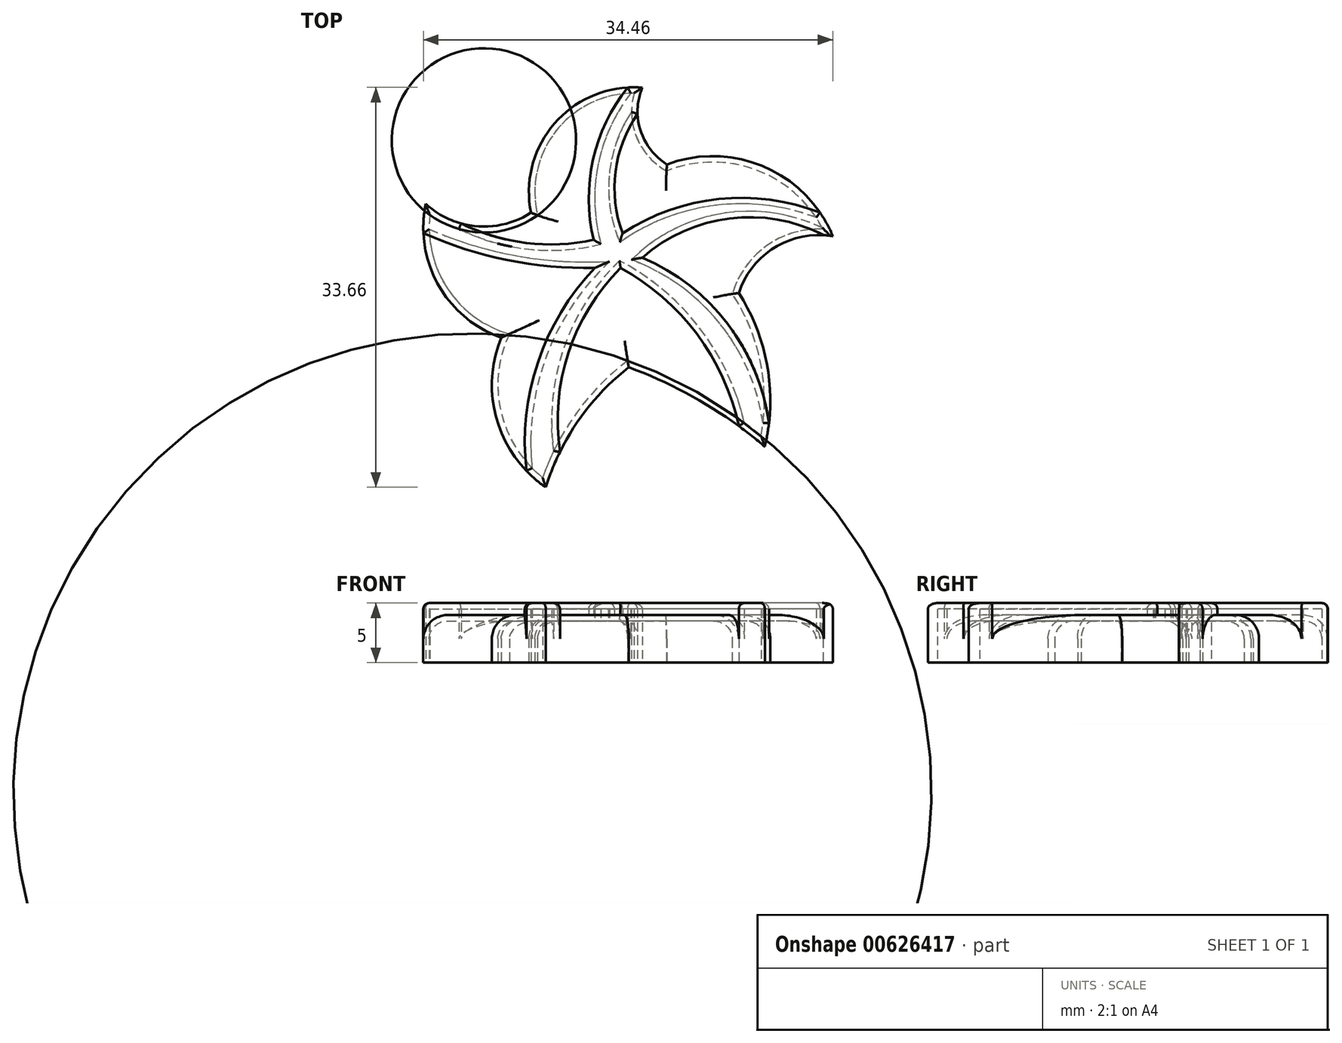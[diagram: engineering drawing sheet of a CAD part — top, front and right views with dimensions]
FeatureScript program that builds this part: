
annotation { "Feature Type Name" : "Feature", "Feature Type Description" : "" }
export const myFeature = defineFeature(function(context is Context, id is Id, definition is map)
    precondition{}
    {
        {
            var Q0;
            Q0=qCreatedBy(makeId("Top.planeOp"),FACE);
            var sketch = newSketch(context, id + "F0", { "sketchPlane" : qUnion([Q0])});
            skArc(sketch, "E0", {"start": v(-51.1, 49.73) * mm, "mid": v(-58.41, 46.8) * mm, "end": v(-60.47, 39.21) * mm});
            skArc(sketch, "E1", {"start": v(-51.1, 49.73) * mm, "mid": v(-51.25, 46.11) * mm, "end": v(-49.02, 43.27) * mm});
            skArc(sketch, "E2", {"start": v(-35.07, 37.23) * mm, "mid": v(-40.83, 43.06) * mm, "end": v(-49.02, 43.27) * mm});
            skArc(sketch, "E3", {"start": v(-35.07, 37.23) * mm, "mid": v(-39.91, 36.3) * mm, "end": v(-42.98, 32.44) * mm});
            skArc(sketch, "E4", {"start": v(-40.8, 19.53) * mm, "mid": v(-40.57, 26.21) * mm, "end": v(-42.98, 32.44) * mm});
            skArc(sketch, "E5", {"start": v(-40.8, 19.53) * mm, "mid": v(-46.23, 23.36) * mm, "end": v(-52.25, 26.2) * mm});
            skArc(sketch, "E6", {"start": v(-52.25, 26.2) * mm, "mid": v(-56.5, 21.68) * mm, "end": v(-59.22, 16.1) * mm});
            skArc(sketch, "E7", {"start": v(-62.97, 28.7) * mm, "mid": v(-63.33, 21.73) * mm, "end": v(-59.22, 16.1) * mm});
            skArc(sketch, "E8", {"start": v(-69.32, 39.94) * mm, "mid": v(-68.27, 33.12) * mm, "end": v(-62.97, 28.7) * mm});
            skArc(sketch, "E9", {"start": v(-69.32, 39.94) * mm, "mid": v(-65.02, 38.06) * mm, "end": v(-60.47, 39.21) * mm});
            skSolve(sketch);
        }
        {
            var Q0;
            Q0=makeQuery(id+"F0.imprint","IMPRINT",FACE,{"disambiguationData":[TD([[makeQuery(id+"F0.imprint","IMPRINT",EDGE,{"derivedFrom":sQuery(id+"F0.wireOp",EDGE,"E0")}),1.0]])]});
            extrude(context, id + "F1", {"entities" : qUnion([Q0]), "depth" : 4 * mm, "offsetDistance" : 25 * mm});
        }
        {
            var Q0;
            Q0=makeQuery(id+"F1.opExtrude","CAP_FACE",FACE,{"disambiguationData":[OSD([sQuery(id+"F0.wireOp",EDGE,"E0"),sQuery(id+"F0.wireOp",EDGE,"E1"),sQuery(id+"F0.wireOp",EDGE,"E2"),sQuery(id+"F0.wireOp",EDGE,"E3"),sQuery(id+"F0.wireOp",EDGE,"E4"),sQuery(id+"F0.wireOp",EDGE,"E5"),sQuery(id+"F0.wireOp",EDGE,"E6"),sQuery(id+"F0.wireOp",EDGE,"E7"),sQuery(id+"F0.wireOp",EDGE,"E8"),sQuery(id+"F0.wireOp",EDGE,"E9")])],"isStart":false});
            var sketch = newSketch(context, id + "F2", { "sketchPlane" : qUnion([Q0])});
            skArc(sketch, "E10", {"start": v(-36.15, 39.21) * mm, "mid": v(-44.66, 40.36) * mm, "end": v(-52.76, 37.48) * mm});
            skArc(sketch, "E11", {"start": v(-35.83, 37.32) * mm, "mid": v(-43.76, 38.73) * mm, "end": v(-51.1, 35.42) * mm});
            skArc(sketch, "E12", {"start": v(-40.45, 21.5) * mm, "mid": v(-43.94, 29.87) * mm, "end": v(-51.1, 35.42) * mm});
            skArc(sketch, "E13", {"start": v(-42.98, 21.25) * mm, "mid": v(-46.5, 28.98) * mm, "end": v(-52.93, 34.56) * mm});
            skArc(sketch, "E14", {"start": v(-52.93, 34.56) * mm, "mid": v(-57.32, 27.42) * mm, "end": v(-58.03, 19.07) * mm});
            skArc(sketch, "E15", {"start": v(-55.11, 34.56) * mm, "mid": v(-59.88, 26.66) * mm, "end": v(-60.86, 17.48) * mm});
            skArc(sketch, "E16", {"start": v(-69.52, 37.48) * mm, "mid": v(-62.48, 35.22) * mm, "end": v(-55.11, 34.56) * mm});
            skArc(sketch, "E17", {"start": v(-66.35, 38.3) * mm, "mid": v(-60.9, 36.66) * mm, "end": v(-55.2, 36.93) * mm});
            skPoint(sketch, "E18.visualSharp", {"position": v(-51.1, 49.73) * mm});
            skArc(sketch, "E19", {"start": v(-52.32, 49.74) * mm, "mid": v(-55.25, 43.67) * mm, "end": v(-55.2, 36.93) * mm});
            skArc(sketch, "E20", {"start": v(-51.5, 47.53) * mm, "mid": v(-53.36, 42.66) * mm, "end": v(-52.76, 37.48) * mm});
            skSolve(sketch);
        }
        {
            var Q0;
            {var subQ9=sQuery(id+"F2.wireOp",EDGE,"E10");Q0=makeQuery(id+"F2.imprint","IMPRINT",FACE,{"disambiguationData":[TD([[makeQuery(id+"F2.imprint","IMPRINT",EDGE,{"derivedFrom":subQ9}),1.0]])]});}
            extrude(context, id + "F3", {"entities" : qUnion([Q0]), "operationType" : NewBodyOperationType.ADD, "depth" : 1 * mm, "offsetDistance" : 25 * mm});
        }
        {
            var Q0;
            Q0=makeQuery(id+"F1.opExtrude","CAP_EDGE",EDGE,{"disambiguationData":[OSD([sQuery(id+"F0.wireOp",EDGE,"E6")])],"isStart":false});
            var Q1;
            Q1=makeQuery(id+"F1.opExtrude","CAP_EDGE",EDGE,{"disambiguationData":[OSD([sQuery(id+"F0.wireOp",EDGE,"E5")])],"isStart":false});
            var Q2;
            Q2=makeQuery(id+"F1.opExtrude","CAP_EDGE",EDGE,{"disambiguationData":[OSD([sQuery(id+"F0.wireOp",EDGE,"E4")])],"isStart":false});
            var Q3;
            Q3=makeQuery(id+"F1.opExtrude","CAP_EDGE",EDGE,{"disambiguationData":[OSD([sQuery(id+"F0.wireOp",EDGE,"E3")])],"isStart":false});
            var Q4;
            Q4=makeQuery(id+"F1.opExtrude","CAP_EDGE",EDGE,{"disambiguationData":[OSD([sQuery(id+"F0.wireOp",EDGE,"E8")])],"isStart":false});
            var Q5;
            Q5=makeQuery(id+"F1.opExtrude","CAP_EDGE",EDGE,{"disambiguationData":[OSD([sQuery(id+"F0.wireOp",EDGE,"E7")])],"isStart":false});
            var Q6;
            Q6=makeQuery(id+"F1.opExtrude","CAP_EDGE",EDGE,{"disambiguationData":[OSD([sQuery(id+"F0.wireOp",EDGE,"E9")])],"isStart":false});
            var Q7;
            Q7=makeQuery(id+"F1.opExtrude","CAP_EDGE",EDGE,{"disambiguationData":[OSD([sQuery(id+"F0.wireOp",EDGE,"E0")])],"isStart":false});
            var Q8;
            Q8=makeQuery(id+"F1.opExtrude","CAP_EDGE",EDGE,{"disambiguationData":[OSD([sQuery(id+"F0.wireOp",EDGE,"E1")])],"isStart":false});
            var Q9;
            Q9=makeQuery(id+"F1.opExtrude","CAP_EDGE",EDGE,{"disambiguationData":[OSD([sQuery(id+"F0.wireOp",EDGE,"E2")])],"isStart":false});
            fillet(context, id + "F4", {"entities" : qUnion([Q0, Q1, Q2, Q3, Q4, Q5, Q6, Q7, Q8, Q9]), "radius" : 2 * mm, "tangentPropagation" : true, "allowEdgeOverflow" : false});
        }
        {
            var Q0;
            Q0=makeQuery(id+"F1.opExtrude","CAP_FACE",FACE,{"disambiguationData":[OSD([sQuery(id+"F0.wireOp",EDGE,"E0"),sQuery(id+"F0.wireOp",EDGE,"E1"),sQuery(id+"F0.wireOp",EDGE,"E2"),sQuery(id+"F0.wireOp",EDGE,"E3"),sQuery(id+"F0.wireOp",EDGE,"E4"),sQuery(id+"F0.wireOp",EDGE,"E5"),sQuery(id+"F0.wireOp",EDGE,"E6"),sQuery(id+"F0.wireOp",EDGE,"E7"),sQuery(id+"F0.wireOp",EDGE,"E8"),sQuery(id+"F0.wireOp",EDGE,"E9")])],"isStart":true});
            shell(context, id + "F5", {"entities" : qUnion([Q0]), "thickness" : 0.5 * mm});
        }
        {
            var Q0;
            Q0=makeQuery(id+"F3.opExtrude","CAP_FACE",FACE,{"disambiguationData":[OSD([sQuery(id+"F0.wireOp",EDGE,"E0"),sQuery(id+"F0.wireOp",EDGE,"E2"),sQuery(id+"F0.wireOp",EDGE,"E3"),sQuery(id+"F0.wireOp",EDGE,"E4"),sQuery(id+"F0.wireOp",EDGE,"E5"),sQuery(id+"F0.wireOp",EDGE,"E6"),sQuery(id+"F0.wireOp",EDGE,"E7"),sQuery(id+"F0.wireOp",EDGE,"E8"),sQuery(id+"F0.wireOp",EDGE,"E9"),sQuery(id+"F2.wireOp",EDGE,"E10"),sQuery(id+"F2.wireOp",EDGE,"E11"),sQuery(id+"F2.wireOp",EDGE,"E12"),sQuery(id+"F2.wireOp",EDGE,"E13"),sQuery(id+"F2.wireOp",EDGE,"E14"),sQuery(id+"F2.wireOp",EDGE,"E15"),sQuery(id+"F2.wireOp",EDGE,"E16"),sQuery(id+"F2.wireOp",EDGE,"E17"),sQuery(id+"F2.wireOp",EDGE,"E19"),sQuery(id+"F2.wireOp",EDGE,"JHTPNBms-L2HQ-8HJM-QWLx-pbRZOle8OsrT")])],"isStart":false});
            fillet(context, id + "F6", {"entities" : qUnion([Q0]), "radius" : 0.5 * mm, "tangentPropagation" : true, "allowEdgeOverflow" : false});
        }
    });
